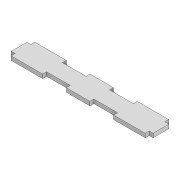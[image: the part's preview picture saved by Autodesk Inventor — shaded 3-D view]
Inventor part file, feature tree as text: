
AUTODESK INVENTOR PART (.ipt)
format: ipt  version: 2022 (Build 260153000, 153)  size: 117,248 bytes
history: native  units: mm
features: extrude x1, sketch x1
ambient origin geometry x8: Origin, YZ Plane, XZ Plane, XY Plane, X Axis, Y Axis, Z Axis, Center Point
bodies: Solid1 (feature_tree)
feature tree (2):
  extrude  "Extrusion1"  Depth=30.0mm
  sketch  "Sketch1"  dims[d0=170.0mm d1=30.0mm d2=5.0mm d3=20.0mm d4=5.0mm d5=5.0mm d6=20.0mm d7=5.0mm d8=5.0mm d9=0.0mm d17=30.0mm d18=5.0mm d19=30.0mm d20=30.0mm d21=15.0mm]
